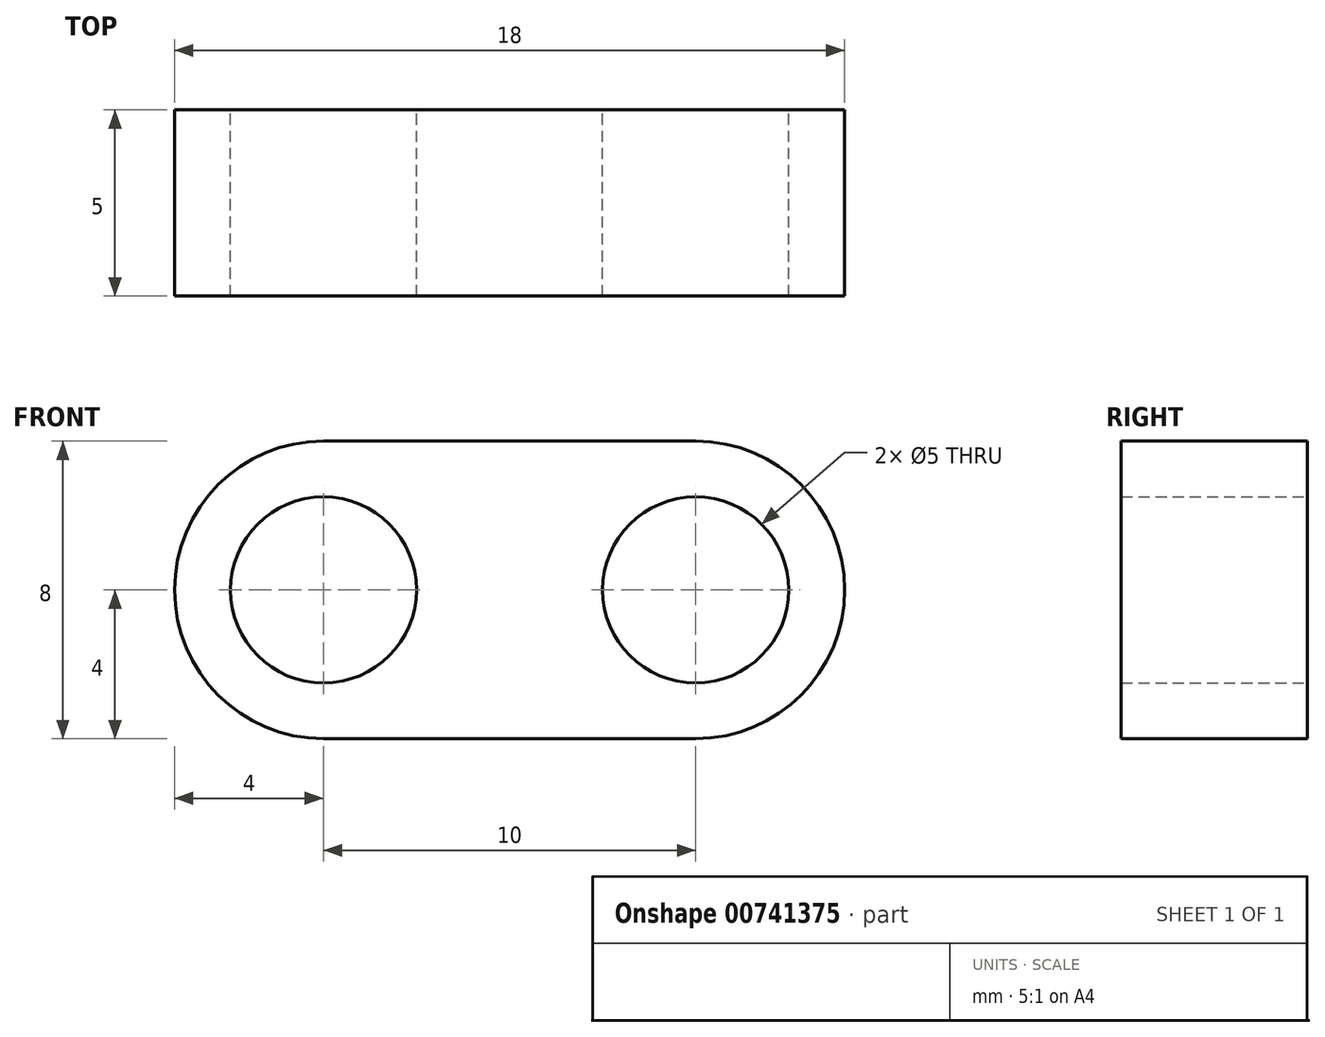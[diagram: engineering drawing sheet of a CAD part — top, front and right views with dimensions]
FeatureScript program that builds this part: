
annotation { "Feature Type Name" : "Feature", "Feature Type Description" : "" }
export const myFeature = defineFeature(function(context is Context, id is Id, definition is map)
    precondition{}
    {
        {
            var Q0;
            Q0=qCreatedBy(makeId("Front.planeOp"),FACE);
            var sketch = newSketch(context, id + "F0", { "sketchPlane" : qUnion([Q0])});
            skArc(sketch, "E0", {"start": v(0, 4) * mm, "mid": v(-4, 0) * mm, "end": v(0, -4) * mm});
            skArc(sketch, "E1", {"start": v(10, -4) * mm, "mid": v(14, 0) * mm, "end": v(10, 4) * mm});
            skLineSegment(sketch, "E2", {"start": v(0, 4) * mm, "end": v(10, 4) * mm});
            skLineSegment(sketch, "E3", {"start": v(0, -4) * mm, "end": v(10, -4) * mm});
            skCircle(sketch, "E4", {"center": v(0, 0) * mm, "radius": 2.5 * mm});
            skCircle(sketch, "E5", {"center": v(10, 0) * mm, "radius": 2.5 * mm});
            skSolve(sketch);
        }
        {
            var Q0;
            Q0=makeQuery(id+"F0.imprint","IMPRINT",FACE,{"disambiguationData":[TD([[makeQuery(id+"F0.imprint","IMPRINT",EDGE,{"derivedFrom":sQuery(id+"F0.wireOp",EDGE,"E0")}),1.0]])]});
            extrude(context, id + "F1", {"entities" : qUnion([Q0]), "depth" : 5 * mm, "offsetDistance" : 25 * mm});
        }
    });
